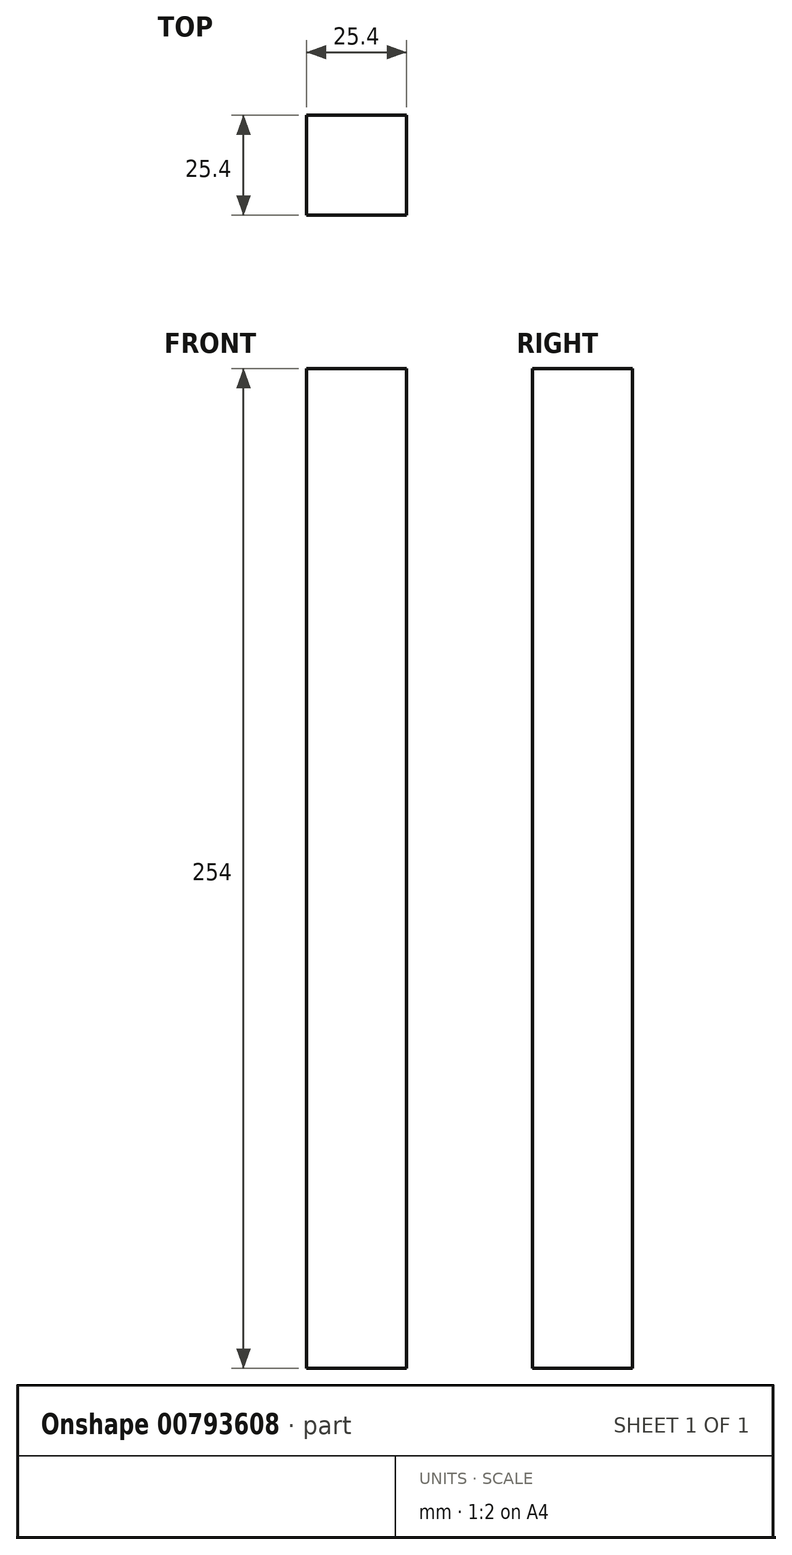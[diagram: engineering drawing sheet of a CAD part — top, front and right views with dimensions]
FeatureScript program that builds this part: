
annotation { "Feature Type Name" : "Feature", "Feature Type Description" : "" }
export const myFeature = defineFeature(function(context is Context, id is Id, definition is map)
    precondition{}
    {
        {
            var Q0;
            Q0=qCreatedBy(makeId("Front.planeOp"),FACE);
            var sketch = newSketch(context, id + "F0", { "sketchPlane" : qUnion([Q0])});
            skLineSegment(sketch, "E0.bottom", {"start": v(0, 0) * mm, "end": v(25.4, 0) * mm});
            skLineSegment(sketch, "E0.top", {"start": v(0, 254) * mm, "end": v(25.4, 254) * mm});
            skLineSegment(sketch, "E0.left", {"start": v(0, 0) * mm, "end": v(0, 254) * mm});
            skLineSegment(sketch, "E0.right", {"start": v(25.4, 0) * mm, "end": v(25.4, 254) * mm});
            skSolve(sketch);
        }
        {
            var Q0;
            Q0 = qSketchRegion(id + "F0", true);
            extrude(context, id + "F1", {"entities" : qUnion([Q0]), "oppositeDirection" : true, "depth" : 25.4 * mm, "offsetDistance" : 25 * mm});
        }
        {
            var Q0;
            Q0=makeQuery(id+"F1.opExtrude","SWEPT_FACE",FACE,{"disambiguationData":[OSD([sQuery(id+"F0.wireOp",EDGE,"E0.top")])]});
            extrude(context, id + "F2", {"entities" : qUnion([Q0]), "operationType" : NewBodyOperationType.ADD, "oppositeDirection" : true, "depth" : 203.2 * mm, "offsetDistance" : 25 * mm});
        }
    });
